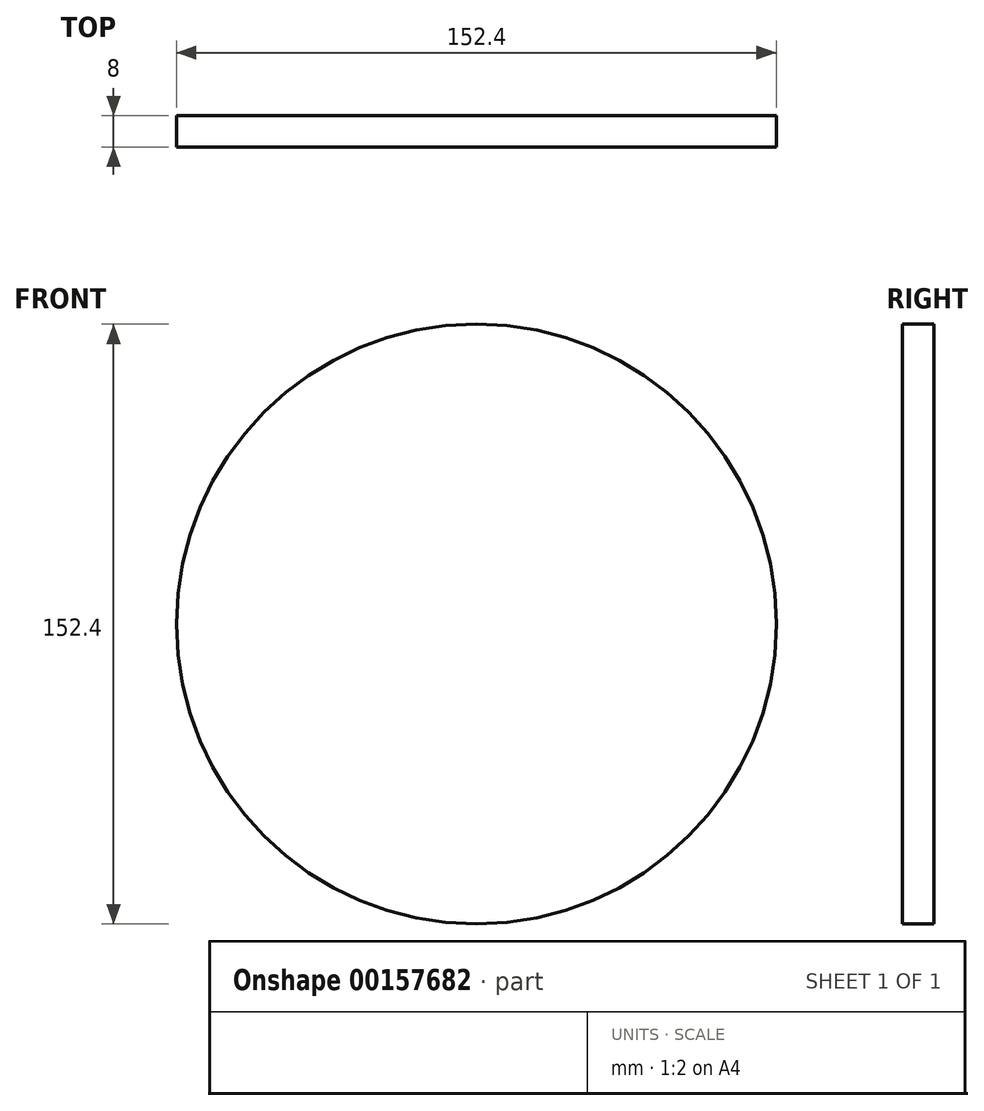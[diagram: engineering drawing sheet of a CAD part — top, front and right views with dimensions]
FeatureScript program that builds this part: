
annotation { "Feature Type Name" : "Feature", "Feature Type Description" : "" }
export const myFeature = defineFeature(function(context is Context, id is Id, definition is map)
    precondition{}
    {
        {
            var Q0;
            Q0=qCreatedBy(makeId("Front.planeOp"),FACE);
            var sketch = newSketch(context, id + "F0", { "sketchPlane" : qUnion([Q0])});
            skCircle(sketch, "E0", {"center": v(0, 0) * mm, "radius": 76.2 * mm});
            skSolve(sketch);
        }
        {
            var Q0;
            Q0 = qSketchRegion(id + "F0", true);
            extrude(context, id + "F1", {"entities" : qUnion([Q0]), "depth" : 8 * mm});
        }
    });
